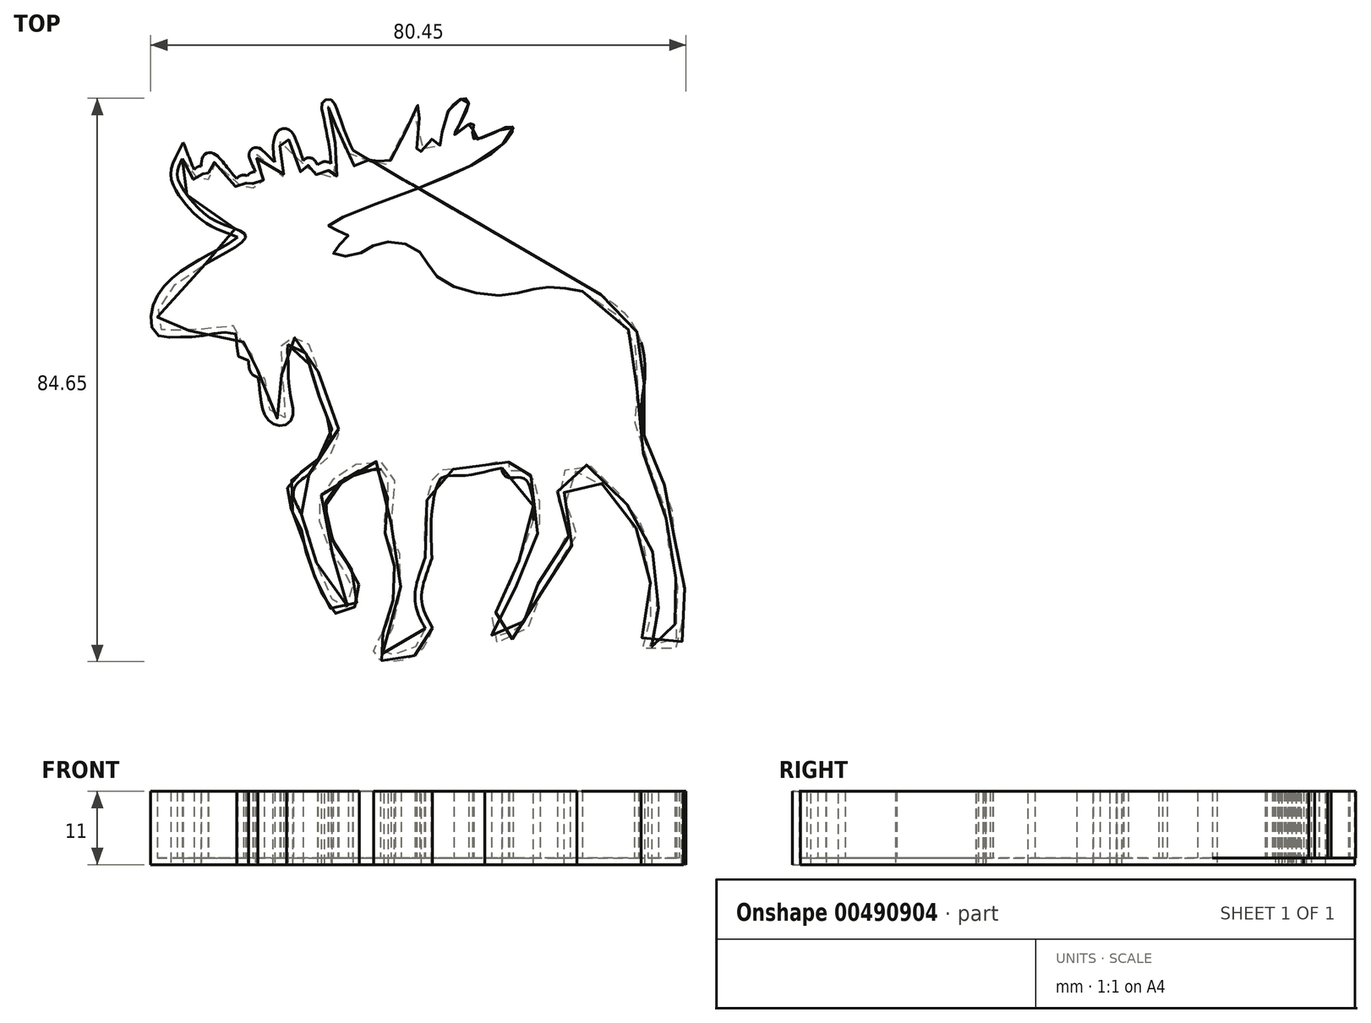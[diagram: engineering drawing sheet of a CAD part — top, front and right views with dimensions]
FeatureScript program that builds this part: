
annotation { "Feature Type Name" : "Feature", "Feature Type Description" : "" }
export const myFeature = defineFeature(function(context is Context, id is Id, definition is map)
    precondition{}
    {
        {
            var Q0;
            Q0=qCreatedBy(makeId("Top.planeOp"),FACE);
            var sketch = newSketch(context, id + "F0", { "sketchPlane" : qUnion([Q0])});
            skFitSpline(sketch, "E0", {"points": [v(-36.5, 38.4) * mm, v(-34.64, 35.3) * mm, v(-33.63, 36.3) * mm, v(-32.63, 35.21) * mm, v(-32.46, 38.32) * mm, v(-28.25, 34.12) * mm, v(-27.33, 34.96) * mm, v(-25.9, 33.87) * mm, v(-25.81, 35.38) * mm, v(-24.22, 35.3) * mm, v(-25.48, 39.08) * mm, v(-21.52, 35.72) * mm, v(-21.86, 39.84) * mm, v(-20.94, 41.85) * mm, v(-18.33, 35.88) * mm, v(-17.49, 37.57) * mm, v(-16.48, 36.05) * mm, v(-15.05, 36.98) * mm, v(-13.7, 35.46) * mm, v(-13.2, 38.4) * mm, v(-14.54, 46.31) * mm, v(-9.92, 36.73) * mm, v(-7.9, 38.74) * mm, v(-5.97, 37.48) * mm, v(-0.92, 46.56) * mm, v(-1.17, 38.91) * mm, v(0.85, 41.35) * mm, v(2.2, 40.43) * mm, v(2.86, 44.3) * mm, v(5.8, 47.49) * mm, v(6.48, 46.31) * mm, v(4.38, 42.02) * mm, v(7.15, 43.79) * mm, v(7.24, 41.43) * mm, v(12.79, 43.28) * mm, v(9.5, 38.91) * mm, v(-14.54, 28.15) * mm, v(-11.6, 26.89) * mm, v(-13.87, 24.45) * mm, v(-10.84, 23.86) * mm, v(-6.64, 25.8) * mm, v(-1, 24.53) * mm, v(1.94, 20.58) * mm, v(11.7, 17.89) * mm, v(17.58, 19.06) * mm, v(23.64, 18.48) * mm], "startDerivative": vector(93.37, -239.58) * mm, "endDerivative": vector(230.3, -44.44) * mm});
            skFitSpline(sketch, "E1", {"points": [v(23.64, 18.48) * mm, v(29.93, 13.62) * mm, v(32.03, 6.28) * mm, v(31.58, -1.96) * mm, v(35.77, -13.2) * mm, v(36.52, -19.8) * mm, v(38.17, -28.48) * mm, v(37.52, -31.44) * mm, v(37.52, -33.98) * mm, v(33.62, -34.73) * mm, v(34.6, -31.51) * mm, v(34.86, -25.77) * mm, v(33.53, -18.56) * mm, v(30.19, -13.36) * mm, v(24.98, -7.88) * mm, v(21.11, -8.28) * mm, v(20.04, -13.09) * mm, v(21.78, -17.5) * mm, v(18.44, -22.84) * mm, v(15.77, -28.44) * mm, v(14.97, -30.84) * mm, v(13.5, -32.45) * mm, v(10.03, -33.25) * mm, v(11.63, -30.04) * mm, v(15.5, -21.23) * mm, v(17.24, -15.76) * mm, v(15.24, -8.68) * mm, v(12.57, -8.42) * mm, v(12.57, -7.22) * mm, v(6.16, -8.15) * mm, v(1.89, -8.68) * mm, v(0, -14.56) * mm, v(0, -21.5) * mm], "startDerivative": vector(187.32, -108.8) * mm, "endDerivative": vector(10.08, -186.6) * mm});
            skFitSpline(sketch, "E2", {"points": [v(0, -21.5) * mm, v(-1.45, -26.17) * mm, v(-1.32, -29.24) * mm, v(0, -32.18) * mm], "startDerivative": vector(-4.74, -12.73) * mm, "endDerivative": vector(4.99, -9.37) * mm});
            skFitSpline(sketch, "E3", {"points": [v(0, -32.18) * mm, v(-2.38, -35.56) * mm, v(-6.66, -35.81) * mm, v(-4.9, -32.18) * mm, v(-4.14, -19.68) * mm, v(-5.15, -17.16) * mm, v(-4.9, -8.6) * mm, v(-9.68, -7.33) * mm, v(-15.23, -11.37) * mm, v(-15.98, -15.65) * mm, v(-13.21, -22.2) * mm, v(-10.94, -26.17) * mm, v(-12.46, -29.26) * mm, v(-15.62, -24.14) * mm, v(-16.96, -20.39) * mm, v(-17.88, -16.5) * mm, v(-19.72, -12.68) * mm, v(-19.3, -10.49) * mm, v(-14.98, -7.02) * mm, v(-13, -3) * mm, v(-13.7, -0.37) * mm, v(-15.93, 5.95) * mm, v(-17.18, 9.95) * mm, v(-18.43, 11.2) * mm, v(-21.28, 11.3) * mm, v(-21.63, 8.62) * mm, v(-21.37, 3.36) * mm, v(-21.1, -0.47) * mm, v(-23.06, 0.06) * mm, v(-24.4, 6.21) * mm, v(-25.38, 6.84) * mm, v(-25.82, 8.97) * mm, v(-27.16, 9.15) * mm, v(-27.7, 12.72) * mm, v(-34.82, 12.63) * mm, v(-37.58, 12.63) * mm, v(-39.81, 12.8) * mm, v(-39.63, 16.9) * mm, v(-32.86, 22.7) * mm, v(-26.98, 26.8) * mm, v(-30.72, 28.67) * mm, v(-34.8, 31.71) * mm, v(-37.12, 35.21) * mm, v(-37.12, 36.98) * mm, v(-36.5, 38.4) * mm], "startDerivative": vector(-64.16, -176.46) * mm, "endDerivative": vector(51.72, 100.17) * mm});
            skSolve(sketch);
        }
        {
            var Q0;
            Q0 = qSketchRegion(id + "FHS7AGOKYNB1j8u_0", true);
            var Q1;
            Q1=makeQuery(id+"F0.imprint","IMPRINT",FACE,{"disambiguationData":[TD([[makeQuery(id+"F0.imprint","IMPRINT",EDGE,{"derivedFrom":sQuery(id+"F0.wireOp",EDGE,"E0")}),-1.0]])]});
            extrude(context, id + "F1", {"entities" : qUnion([Q0, Q1]), "depth" : 10 * mm});
        }
        {
            var Q0;
            Q0=makeQuery(id+"F1.opExtrude","CAP_FACE",FACE,{"disambiguationData":[OSD([sQuery(id+"F0.wireOp",EDGE,"E0"),sQuery(id+"F0.wireOp",EDGE,"E1"),sQuery(id+"F0.wireOp",EDGE,"E2"),sQuery(id+"F0.wireOp",EDGE,"E3")])],"isStart":false});
            shell(context, id + "F2", {"entities" : qUnion([Q0]), "thickness" : 1 * mm, "oppositeDirection" : true});
        }
    });
